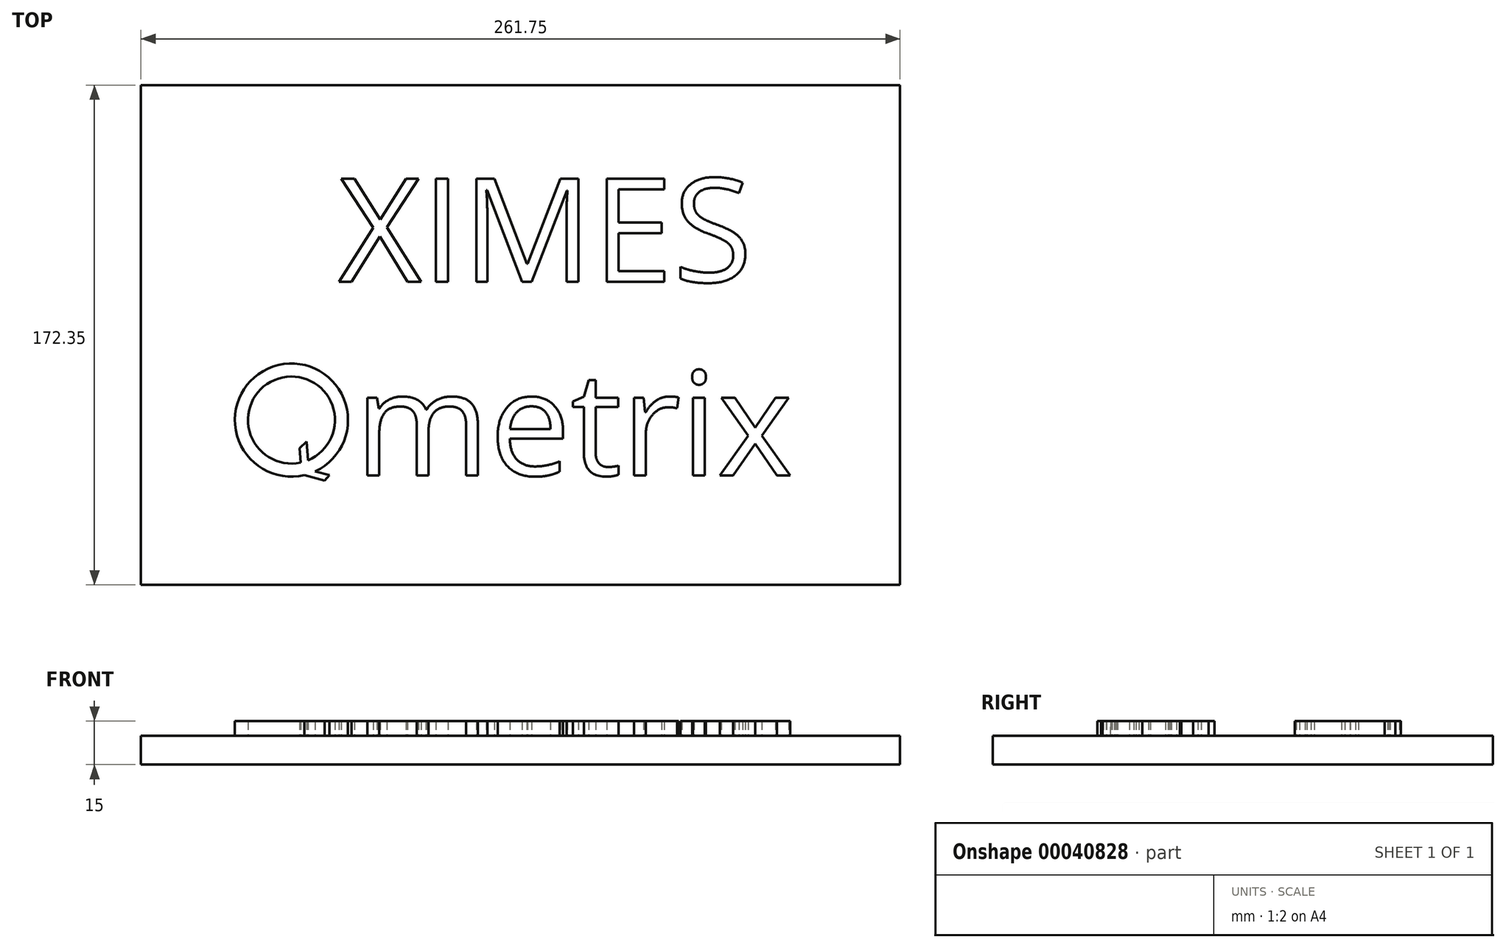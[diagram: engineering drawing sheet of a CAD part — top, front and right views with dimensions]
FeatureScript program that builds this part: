
annotation { "Feature Type Name" : "Feature", "Feature Type Description" : "" }
export const myFeature = defineFeature(function(context is Context, id is Id, definition is map)
    precondition{}
    {
        {
            var Q0;
            Q0=qCreatedBy(makeId("Top.planeOp"),FACE);
            var sketch = newSketch(context, id + "F0", { "sketchPlane" : qUnion([Q0])});
            skText(sketch, "E0", { "text": "metrix", "fontName": "OpenSans-Regular.ttf"});
            skLineSegment(sketch, "E1", {"start": v(-46.28, -37.98) * mm, "end": v(-46.66, -33.07) * mm});
            skLineSegment(sketch, "E2", {"start": v(-46.66, -33.07) * mm, "end": v(-44.25, -30.77) * mm});
            skLineSegment(sketch, "E3", {"start": v(-44.25, -30.77) * mm, "end": v(-43.75, -37.19) * mm});
            skArc(sketch, "E4", {"start": v(-41.27, -41.02) * mm, "mid": v(-55.8, -4.87) * mm, "end": v(-45.06, -42.32) * mm});
            skArc(sketch, "E5", {"start": v(-43.75, -37.19) * mm, "mid": v(-53.94, -9) * mm, "end": v(-46.28, -37.98) * mm});
            skLineSegment(sketch, "E6", {"start": v(-41.27, -41.02) * mm, "end": v(-36.37, -42.32) * mm});
            skPoint(sketch, "E6.endSnap0", {"position": v(-45.06, -42.32) * mm});
            skLineSegment(sketch, "E7", {"start": v(-36.37, -42.32) * mm, "end": v(-38, -44.2) * mm});
            skLineSegment(sketch, "E8", {"start": v(-38, -44.2) * mm, "end": v(-45.06, -42.32) * mm});
            skText(sketch, "E9", { "text": "XIMES", "fontName": "OpenSans-Regular.ttf"});
            skLineSegment(sketch, "E10.rect.bottom", {"start": v(160.42, -80.18) * mm, "end": v(-101.33, -80.18) * mm});
            skLineSegment(sketch, "E10.rect.top", {"start": v(160.42, 92.17) * mm, "end": v(-101.33, 92.17) * mm});
            skLineSegment(sketch, "E10.rect.left", {"start": v(160.42, -80.18) * mm, "end": v(160.42, 92.17) * mm});
            skLineSegment(sketch, "E10.rect.right", {"start": v(-101.33, -80.18) * mm, "end": v(-101.33, 92.17) * mm});
            skPoint(sketch, "E10.rect.middle", {"position": v(29.54, 6) * mm});
            const initialGuessF0  = {"E0": [-0.02752, -0.04238, 1, 0, 0.03589], "E9": [-0.0333, 0.02438, 1, 0, 0.03589]};
            skSetInitialGuess(sketch, initialGuessF0);
            skSolve(sketch);
        }
        {
            var Q0;
            Q0=makeQuery(id+"F0.imprint","IMPRINT",FACE,{"disambiguationData":[TD([[makeQuery(id+"F0.imprint","IMPRINT",EDGE,{"derivedFrom":sQuery(id+"F0.wireOp",EDGE,"E0.sketch_text.stroke-0")}),1.0]])]});
            var Q1;
            Q1=makeQuery(id+"F0.imprint","IMPRINT",FACE,{"disambiguationData":[TD([[makeQuery(id+"F0.imprint","IMPRINT",EDGE,{"derivedFrom":sQuery(id+"F0.wireOp",EDGE,"E1")}),1.0]])]});
            var Q2;
            Q2=makeQuery(id+"F0.imprint","IMPRINT",FACE,{"disambiguationData":[TD([[makeQuery(id+"F0.imprint","IMPRINT",EDGE,{"derivedFrom":sQuery(id+"F0.wireOp",EDGE,"E0.sketch_text.stroke-42")}),1.0]])]});
            extrude(context, id + "F1", {"entities" : qUnion([Q0, Q1, Q2]), "depth" : 10 * mm});
        }
        {
            var Q0;
            Q0=makeQuery(id+"F0.imprint","IMPRINT",FACE,{"disambiguationData":[TD([[makeQuery(id+"F0.imprint","IMPRINT",EDGE,{"derivedFrom":sQuery(id+"F0.wireOp",EDGE,"E1")}),-1.0]])]});
            var Q1;
            Q1=makeQuery(id+"F0.imprint","IMPRINT",FACE,{"disambiguationData":[TD([[makeQuery(id+"F0.imprint","IMPRINT",EDGE,{"derivedFrom":sQuery(id+"F0.wireOp",EDGE,"E0.sketch_text.stroke-0")}),-1.0]])]});
            var Q2;
            Q2=makeQuery(id+"F0.imprint","IMPRINT",FACE,{"disambiguationData":[TD([[makeQuery(id+"F0.imprint","IMPRINT",EDGE,{"derivedFrom":sQuery(id+"F0.wireOp",EDGE,"E0.sketch_text.stroke-28")}),-1.0]])]});
            var Q3;
            Q3=makeQuery(id+"F0.imprint","IMPRINT",FACE,{"disambiguationData":[TD([[makeQuery(id+"F0.imprint","IMPRINT",EDGE,{"derivedFrom":sQuery(id+"F0.wireOp",EDGE,"E0.sketch_text.stroke-47")}),-1.0]])]});
            var Q4;
            Q4=makeQuery(id+"F0.imprint","IMPRINT",FACE,{"disambiguationData":[TD([[makeQuery(id+"F0.imprint","IMPRINT",EDGE,{"derivedFrom":sQuery(id+"F0.wireOp",EDGE,"E0.sketch_text.stroke-66")}),-1.0]])]});
            var Q5;
            Q5=makeQuery(id+"F0.imprint","IMPRINT",FACE,{"disambiguationData":[TD([[makeQuery(id+"F0.imprint","IMPRINT",EDGE,{"derivedFrom":sQuery(id+"F0.wireOp",EDGE,"E0.sketch_text.stroke-79")}),-1.0]])]});
            var Q6;
            Q6=makeQuery(id+"F0.imprint","IMPRINT",FACE,{"disambiguationData":[TD([[makeQuery(id+"F0.imprint","IMPRINT",EDGE,{"derivedFrom":sQuery(id+"F0.wireOp",EDGE,"E0.sketch_text.stroke-91")}),-1.0]])]});
            var Q7;
            Q7=makeQuery(id+"F0.imprint","IMPRINT",FACE,{"disambiguationData":[TD([[makeQuery(id+"F0.imprint","IMPRINT",EDGE,{"derivedFrom":sQuery(id+"F0.wireOp",EDGE,"E0.sketch_text.stroke-83")}),-1.0]])]});
            var Q8;
            Q8=makeQuery(id+"F0.imprint","IMPRINT",FACE,{"disambiguationData":[TD([[makeQuery(id+"F0.imprint","IMPRINT",EDGE,{"derivedFrom":sQuery(id+"F0.wireOp",EDGE,"E9.sketch_text.stroke-34")}),-1.0]])]});
            var Q9;
            Q9=makeQuery(id+"F0.imprint","IMPRINT",FACE,{"disambiguationData":[TD([[makeQuery(id+"F0.imprint","IMPRINT",EDGE,{"derivedFrom":sQuery(id+"F0.wireOp",EDGE,"E9.sketch_text.stroke-46")}),-1.0]])]});
            var Q10;
            Q10=makeQuery(id+"F0.imprint","IMPRINT",FACE,{"disambiguationData":[TD([[makeQuery(id+"F0.imprint","IMPRINT",EDGE,{"derivedFrom":sQuery(id+"F0.wireOp",EDGE,"E9.sketch_text.stroke-16")}),-1.0]])]});
            var Q11;
            Q11=makeQuery(id+"F0.imprint","IMPRINT",FACE,{"disambiguationData":[TD([[makeQuery(id+"F0.imprint","IMPRINT",EDGE,{"derivedFrom":sQuery(id+"F0.wireOp",EDGE,"E9.sketch_text.stroke-12")}),-1.0]])]});
            var Q12;
            Q12=makeQuery(id+"F0.imprint","IMPRINT",FACE,{"disambiguationData":[TD([[makeQuery(id+"F0.imprint","IMPRINT",EDGE,{"derivedFrom":sQuery(id+"F0.wireOp",EDGE,"E9.sketch_text.stroke-0")}),-1.0]])]});
            extrude(context, id + "F2", {"entities" : qUnion([Q0, Q1, Q2, Q3, Q4, Q5, Q6, Q7, Q8, Q9, Q10, Q11, Q12]), "operationType" : NewBodyOperationType.ADD, "depth" : 15 * mm});
        }
    });
